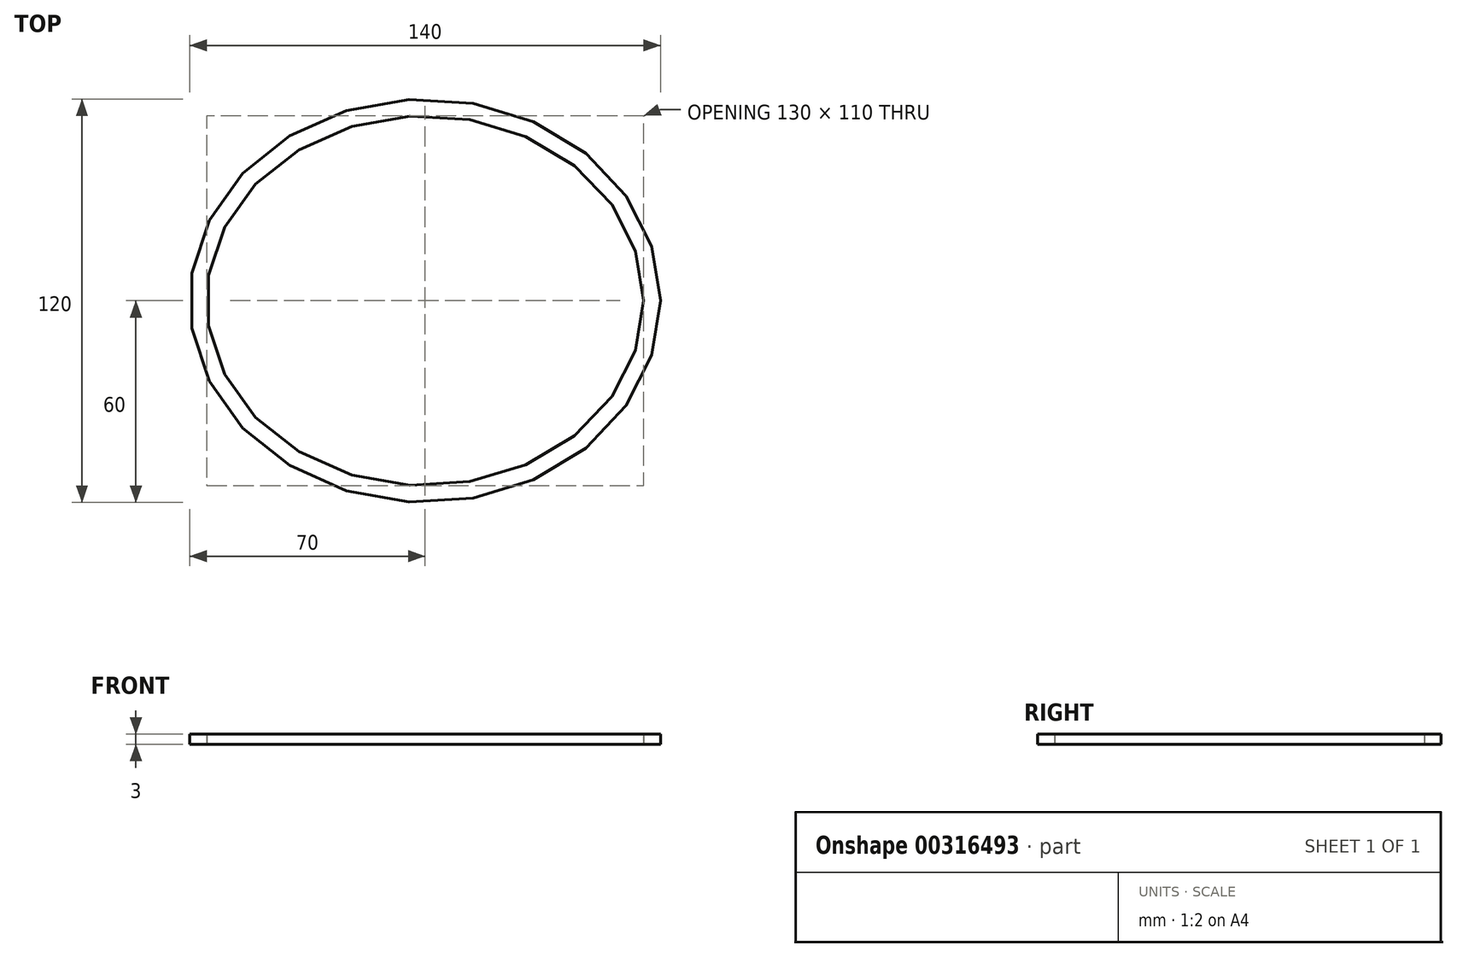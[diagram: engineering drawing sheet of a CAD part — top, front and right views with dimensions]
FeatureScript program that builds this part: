
annotation { "Feature Type Name" : "Feature", "Feature Type Description" : "" }
export const myFeature = defineFeature(function(context is Context, id is Id, definition is map)
    precondition{}
    {
        {
            var Q0;
            Q0=qCreatedBy(makeId("Top.planeOp"),FACE);
            var sketch = newSketch(context, id + "F0", { "sketchPlane" : qUnion([Q0])});
            skLineSegment(sketch, "E0", {"start": v(0, 0) * mm, "end": v(70, 0) * mm});
            skLineSegment(sketch, "E1", {"start": v(0, 0) * mm, "end": v(0, 60) * mm});
            skEllipse(sketch, "E2", {"center": v(0, 0) * mm, "majorRadius": 70 * mm, "minorRadius": 60 * mm, "majorAxis": v(1, 0)});
            skLineSegment(sketch, "E3", {"start": v(70, 0) * mm, "end": v(65, 0) * mm});
            skLineSegment(sketch, "E4", {"start": v(0, 60) * mm, "end": v(0, 55) * mm});
            skEllipse(sketch, "E5", {"center": v(0, 0) * mm, "majorRadius": 65 * mm, "minorRadius": 55 * mm, "majorAxis": v(1, 0)});
            skSolve(sketch);
        }
        {
            var Q0;
            {var subQ0=sQuery(id+"F0.wireOp",EDGE,"E2");var subQ1=sQuery(id+"F0.wireOp",EDGE,"E0");var subQ2=makeQuery(id+"F0.imprint","INTERSECT",VERTEX,{"derivedFrom":[subQ1,subQ0]});Q0=makeQuery(id+"F0.imprint","IMPRINT",FACE,{"disambiguationData":[TD([[makeQuery(id+"F0.imprint","IMPRINT",EDGE,{"disambiguationData":[TD([[subQ2,1.0]])],"derivedFrom":subQ1}),-1.0]])]});}
            var Q1;
            {var subQ0=sQuery(id+"F0.wireOp",EDGE,"E2");var subQ1=sQuery(id+"F0.wireOp",EDGE,"E0");var subQ2=makeQuery(id+"F0.imprint","INTERSECT",VERTEX,{"derivedFrom":[subQ1,subQ0]});Q1=makeQuery(id+"F0.imprint","IMPRINT",FACE,{"disambiguationData":[TD([[makeQuery(id+"F0.imprint","IMPRINT",EDGE,{"disambiguationData":[TD([[subQ2,1.0]])],"derivedFrom":subQ1}),1.0]])]});}
            extrude(context, id + "F1", {"entities" : qUnion([Q0, Q1]), "depth" : 3 * mm});
        }
    });
